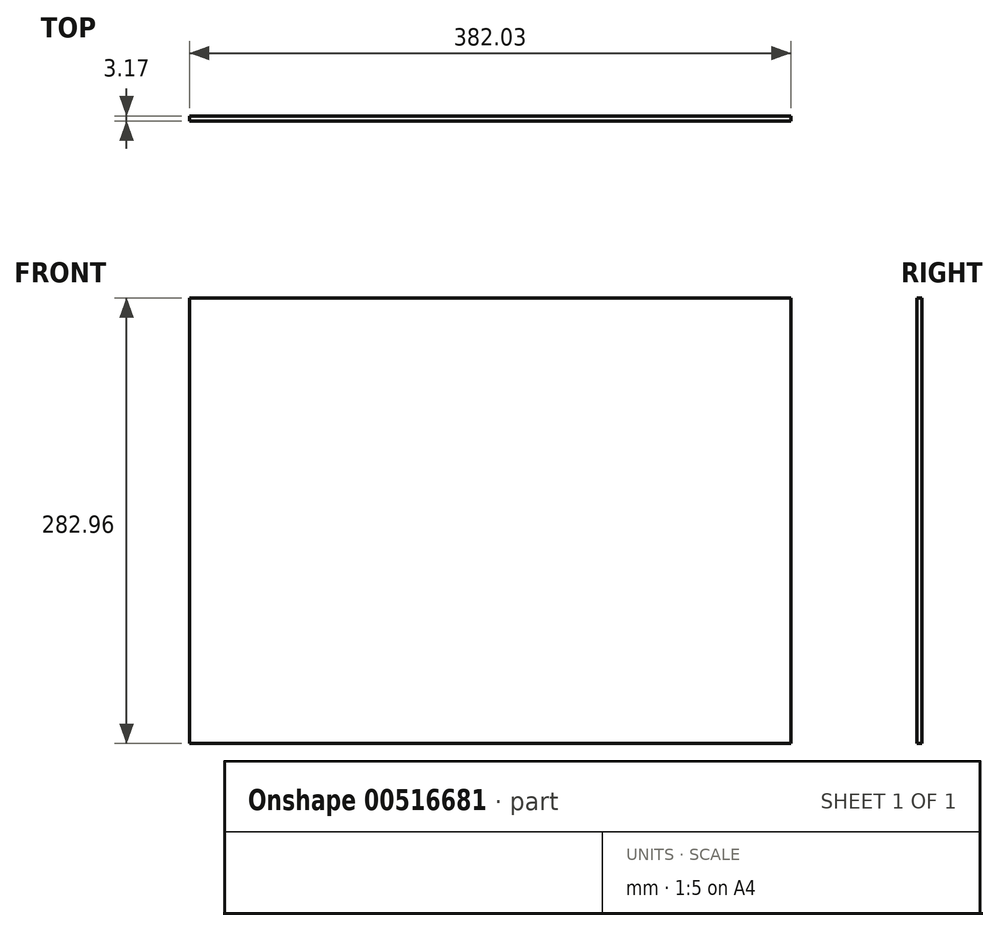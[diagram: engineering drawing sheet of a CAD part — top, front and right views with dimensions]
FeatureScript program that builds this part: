
annotation { "Feature Type Name" : "Feature", "Feature Type Description" : "" }
export const myFeature = defineFeature(function(context is Context, id is Id, definition is map)
    precondition{}
    {
        {
            var Q0;
            Q0=qCreatedBy(makeId("Front.planeOp"),FACE);
            var sketch = newSketch(context, id + "F0", { "sketchPlane" : qUnion([Q0])});
            skLineSegment(sketch, "E0.bottom", {"start": v(0, 0) * mm, "end": v(382.03, 0) * mm});
            skLineSegment(sketch, "E0.top", {"start": v(0, 282.96) * mm, "end": v(382.03, 282.96) * mm});
            skLineSegment(sketch, "E0.left", {"start": v(0, 0) * mm, "end": v(0, 282.96) * mm});
            skLineSegment(sketch, "E0.right", {"start": v(382.03, 0) * mm, "end": v(382.03, 282.96) * mm});
            skSolve(sketch);
        }
        {
            var Q0;
            Q0=makeQuery(id+"F0.imprint","IMPRINT",FACE,{"disambiguationData":[TD([[makeQuery(id+"F0.imprint","IMPRINT",EDGE,{"derivedFrom":sQuery(id+"F0.wireOp",EDGE,"E0.bottom")}),1.0]])]});
            extrude(context, id + "F1", {"entities" : qUnion([Q0]), "depth" : 3.17 * mm, "offsetDistance" : 25.4 * mm});
        }
    });
